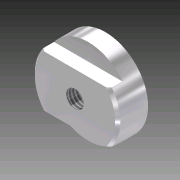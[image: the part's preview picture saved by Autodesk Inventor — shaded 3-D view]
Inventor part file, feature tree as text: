
AUTODESK INVENTOR PART (.ipt)
format: ipt  version: 2011 (Build 150239000, 239)  size: 98,304 bytes
history: native  units: in
note: dims shown in document units (in); Inventor stores cm internally (conversion verified against a paired STEP export)
features: extrude x3, sketch x3, chamfer x1, thread x1
ambient origin geometry x8: Origin, YZ Plane, XZ Plane, XY Plane, X Axis, Y Axis, Z Axis, Center Point
bodies: Solid1 (feature_tree)
feature tree (8):
  extrude  "Extrusion1"  Depth=0.737in TaperAngle=0.0deg
  chamfer  "Chamfer1"  Distance=0.0625in Angle=45.0deg
  extrude  "Extrusion2"  Depth=0.625in
  extrude  "Extrusion3"  Depth=0.425in
  thread  "Thread1"  [1 undecoded]
  sketch  "Sketch1"  dims[d0=2.082in d1=0.737in d2=0.0in d3=0.0625in d4=0.125in d5=45.0deg]
  sketch  "Sketch2"  dims[d6=1.25in d7=0.625in]
  sketch  "Sketch3"  dims[d8=0.32in d9=0.0in d10=0.425in d11=0.32in d12=0.0in d13=1.0in d14=0.0in]
note: 1 required parameter value undecoded (feature->parameter linkage not recoverable at this tier; creation-order binding heuristic only, values carry confidence <= 0.55)
